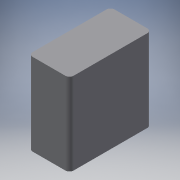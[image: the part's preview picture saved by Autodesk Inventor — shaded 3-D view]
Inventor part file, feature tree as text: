
AUTODESK INVENTOR PART (.ipt)
format: ipt  version: 2016 (Build 200138000, 138)  size: 101,376 bytes
history: native  units: mm
features: reference x3, extrude x2, sketch x2
ambient origin geometry x8: Origin, YZ Plane, XZ Plane, XY Plane, X Axis, Y Axis, Z Axis, Center Point
bodies: Solid1 (feature_tree)
feature tree (7):
  extrude  "Extrusion1"  Depth=40.0mm TaperAngle=0.0deg
  extrude  "Extrusion2"  [1 undecoded]
  sketch  "Sketch1"  dims[d0=0.0mm d1=40.0mm d2=0.0mm]
  reference  "Reference1"
  sketch  "Sketch2"  dims[d3=30.0mm d4=0.0mm]
  reference  "Reference2"
  reference  "Reference3"
note: 1 required parameter value undecoded (feature->parameter linkage not recoverable at this tier; creation-order binding heuristic only, values carry confidence <= 0.55)
